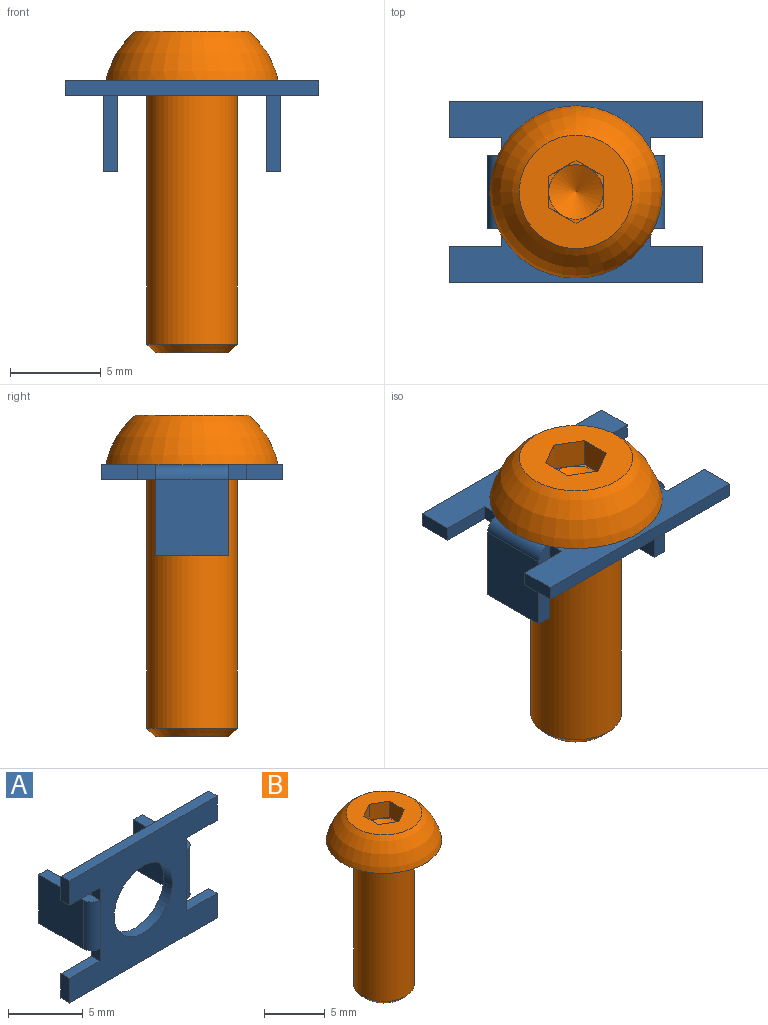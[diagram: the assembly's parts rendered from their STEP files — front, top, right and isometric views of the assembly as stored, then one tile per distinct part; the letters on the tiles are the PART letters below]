
ASSEMBLY  parts=2 mates=1
PART A: 29 faces, bbox 14x5x10 mm
  f0: plane 14x10mm, normal (0,-1,0), area 81.4mm2, adj f3,f4,f5,f6,f7,f9,f10,f13
  f1: plane 4.2x4mm, normal (-1,0,0), area 16.8mm2, adj f2,f11,f18,f19
  f2: plane 14x10mm, normal (0,1,0), area 81.4mm2, adj f1,f3,f4,f5,f6,f7,f8,f9
  f3: plane 1x0.8mm, normal (1,0,0), area 0.8mm2, adj f0,f2,f6,f18
  f4: plane 1x0.8mm, normal (-1,0,0), area 0.8mm2, adj f0,f2,f16,f20
  f5: plane 1x0.8mm, normal (1,0,0), area 0.8mm2, adj f0,f2,f7,f19
  f6: plane 2.9x0.8mm, normal (0,0,1), area 2.3mm2, adj f0,f2,f3,f24
  f7: plane 2.9x0.8mm, normal (0,0,-1), area 2.3mm2, adj f0,f2,f5,f25
  f8: plane 4.2x4mm, normal (1,0,0), area 16.8mm2, adj f2,f15,f16,f17
  f9: cylinder r=2.75mm len=5.5mm, axis (0,1,0), area 13.8mm2, adj f0,f2
  f10: cylinder r=0.8mm len=4mm, axis (0,0,1), area 5mm2, adj f0,f14,f16,f17
  f11: plane 4x0.8mm, normal (0,1,0), area 3.2mm2, adj f1,f12,f18,f19
  f12: plane 4.2x4mm, normal (1,0,0), area 16.8mm2, adj f11,f13,f18,f19
  f13: cylinder r=0.8mm len=4mm, axis (0,0,1), area 5mm2, adj f0,f12,f18,f19
  f14: plane 4.2x4mm, normal (-1,0,0), area 16.8mm2, adj f10,f15,f16,f17
  f15: plane 4x0.8mm, normal (0,1,0), area 3.2mm2, adj f8,f14,f16,f17
  f16: plane 5x0.8mm, normal (0,0,-1), area 3.9mm2, adj f4,f8,f10,f14,f15
  f17: plane 5x0.8mm, normal (0,0,1), area 3.9mm2, adj f8,f10,f14,f15,f21
  f18: plane 5x0.8mm, normal (0,0,-1), area 3.9mm2, adj f1,f3,f11,f12,f13
  f19: plane 5x0.8mm, normal (0,0,1), area 3.9mm2, adj f1,f5,f11,f12,f13
  f20: plane 2.9x0.8mm, normal (0,0,1), area 2.3mm2, adj f0,f2,f4,f22
  f21: plane 1x0.8mm, normal (-1,0,0), area 0.8mm2, adj f0,f2,f17,f28
  f22: plane 2x0.8mm, normal (-1,0,0), area 1.6mm2, adj f0,f2,f20,f23
  f23: plane 14x0.8mm, normal (0,0,-1), area 11.2mm2, adj f0,f2,f22,f24
  f24: plane 2x0.8mm, normal (1,0,0), area 1.6mm2, adj f0,f2,f6,f23
  f25: plane 2x0.8mm, normal (1,0,0), area 1.6mm2, adj f0,f2,f7,f26
  f26: plane 14x0.8mm, normal (0,0,1), area 11.2mm2, adj f0,f2,f25,f27
  f27: plane 2x0.8mm, normal (-1,0,0), area 1.6mm2, adj f0,f2,f26,f28
  f28: plane 2.9x0.8mm, normal (0,0,-1), area 2.3mm2, adj f0,f2,f21,f27
PART B: 20 faces, bbox 9.5x9.5x17.8 mm
  f0: plane 1.3x0.75mm, normal (0,0,1), area 0.1mm2, adj f12,f13,f16
  f1: plane 1.5x0.43mm, normal (0,0,1), area 0.1mm2, adj f11,f12,f16
  f2: plane 4.02x4.02mm, normal (0,0,-1), area 12.7mm2, adj f9
  f3: plane 1.3x0.75mm, normal (0,0,1), area 0.1mm2, adj f13,f14,f16
  f4: plane 6.25x6.25mm, normal (0,0,1), area 22.9mm2, adj f5,f10,f11,f12,f13,f14,f15
  f5: torus R=0.09mm, axis (0,0,-1), area 83.8mm2, adj f4,f6
  f6: plane 9.5x9.5mm, normal (0,0,-1), area 40.7mm2, adj f5,f7
  f7: torus R=3.1mm, axis (0,0,-1), area 16.1mm2, adj f6,f8
  f8: cylinder r=2.5mm len=13.91mm, axis (0,0,1), area 218.5mm2, adj f7,f9
  f9: cone r=2.5mm half-angle=45deg, axis (0,0,1), area 9.8mm2, adj f2,f8
  f10: plane 1.73x1.6mm, normal (1,0,0), area 2.8mm2, adj f4,f11,f15,f18,f19
  f11: plane 1.6x1.5mm, normal (0.5,0.87,0), area 2.8mm2, adj f1,f4,f10,f12,f19
  f12: plane 1.6x1.5mm, normal (-0.5,0.87,0), area 2.8mm2, adj f0,f1,f4,f11,f13
  f13: plane 1.73x1.6mm, normal (-1,0,0), area 2.8mm2, adj f0,f3,f4,f12,f14
  f14: plane 1.6x1.5mm, normal (-0.5,-0.87,0), area 2.8mm2, adj f3,f4,f13,f15,f17
  f15: plane 1.6x1.5mm, normal (0.5,-0.87,0), area 2.8mm2, adj f4,f10,f14,f17,f18
  f16: cone r=866.03mm half-angle=60deg, axis (0,0,1), area 8.2mm2, adj f0,f1,f3,f17,f18,f19
  f17: plane 1.5x0.43mm, normal (0,0,1), area 0.1mm2, adj f14,f15,f16
  f18: plane 1.3x0.75mm, normal (0,0,1), area 0.1mm2, adj f10,f15,f16
  f19: plane 1.3x0.75mm, normal (0,0,1), area 0.1mm2, adj f10,f11,f16
PLACE A rot(axis=(-1,0,0),90deg) t=(0,0,-1.6)mm fixed
PLACE B t=(0,0,-1.6)mm
MATE fastened B.f8 <-> A.f9  axis (0,0,-1) through (0,0,-1.6)mm
